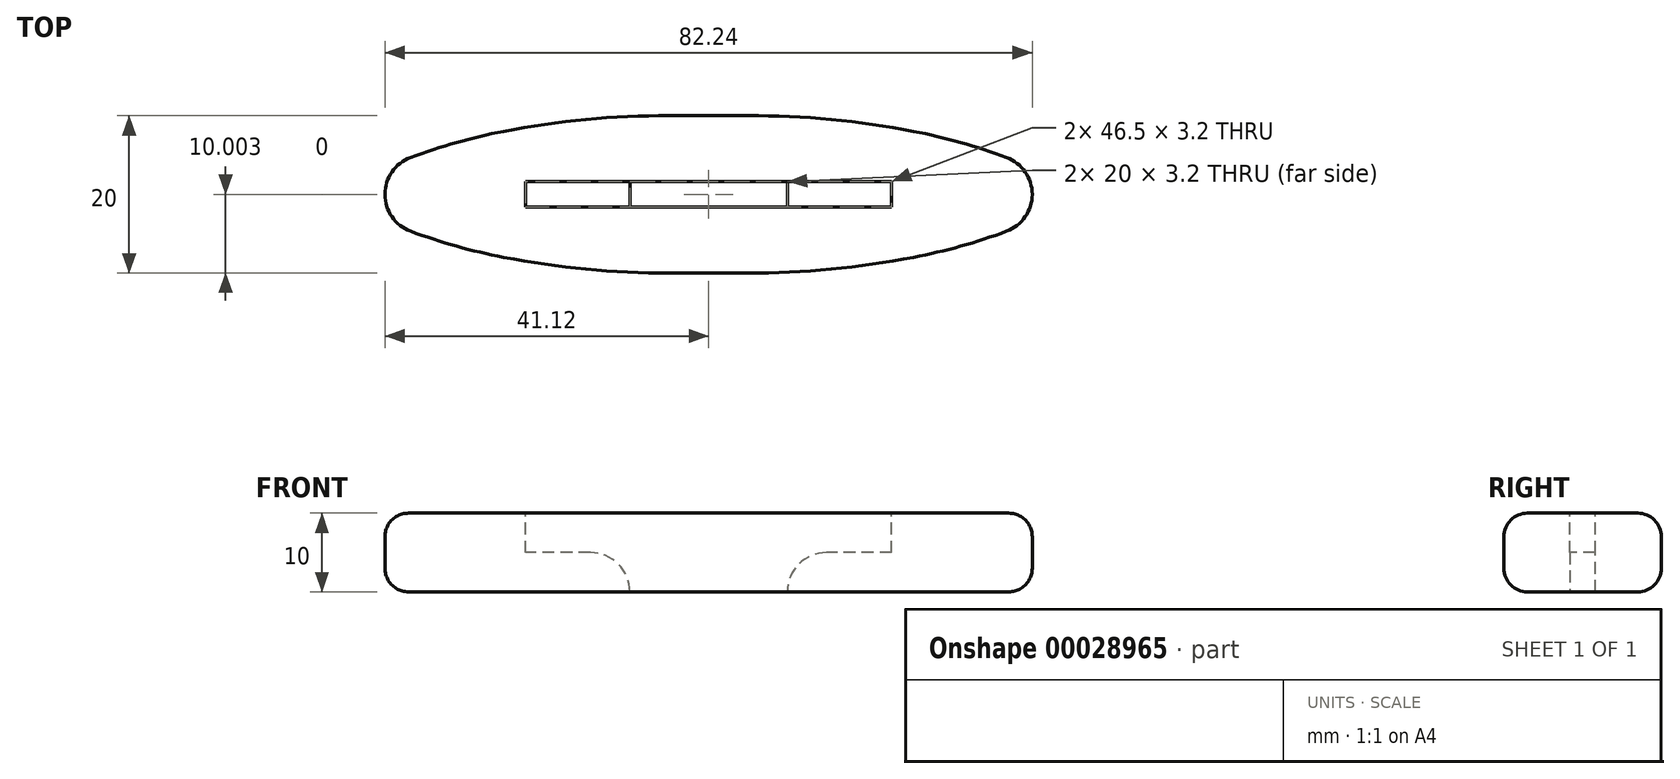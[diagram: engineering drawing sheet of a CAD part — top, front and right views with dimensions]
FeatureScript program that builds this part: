
annotation { "Feature Type Name" : "Feature", "Feature Type Description" : "" }
export const myFeature = defineFeature(function(context is Context, id is Id, definition is map)
    precondition{}
    {
        {
            var Q0;
            Q0=qCreatedBy(makeId("Top.planeOp"),FACE);
            var sketch = newSketch(context, id + "F0", { "sketchPlane" : qUnion([Q0])});
            skLineSegment(sketch, "E0", {"start": v(0, 0) * mm, "end": v(0, 63.05) * mm, "construction": true});
            skPoint(sketch, "E1", {"position": v(0, 31.52) * mm});
            skLineSegment(sketch, "E2.bottom", {"start": v(0, 31.52) * mm, "end": v(-10, 31.52) * mm});
            skLineSegment(sketch, "E2.top", {"start": v(0, 34.72) * mm, "end": v(-10, 34.72) * mm});
            skLineSegment(sketch, "E2.left", {"start": v(0, 31.52) * mm, "end": v(0, 34.72) * mm});
            skLineSegment(sketch, "E2.right", {"start": v(-10, 31.52) * mm, "end": v(-10, 34.72) * mm});
            skPoint(sketch, "E3", {"position": v(0, 33.12) * mm});
            skPoint(sketch, "E4", {"position": v(-48, 33.12) * mm});
            skLineSegment(sketch, "E5", {"start": v(0, 33.12) * mm, "end": v(-68.68, 33.12) * mm, "construction": true});
            skPoint(sketch, "E6", {"position": v(0, 43.12) * mm});
            skPoint(sketch, "E7", {"position": v(-26.03, 41.12) * mm});
            skPoint(sketch, "E8", {"position": v(-5, 43.12) * mm});
            skLineSegment(sketch, "E9", {"start": v(0, 43.12) * mm, "end": v(-5, 43.12) * mm});
            skArc(sketch, "E10", {"start": v(-5, 43.12) * mm, "mid": v(-15.56, 42.62) * mm, "end": v(-26.03, 41.12) * mm});
            skArc(sketch, "E11", {"start": v(-26.03, 41.12) * mm, "mid": v(-37.34, 38) * mm, "end": v(-48, 33.12) * mm});
            skArc(sketch, "E12.MirrorCS", {"start": v(-26.03, 25.12) * mm, "mid": v(-37.34, 28.24) * mm, "end": v(-48, 33.12) * mm});
            skArc(sketch, "E13.MirrorCS", {"start": v(-5, 23.12) * mm, "mid": v(-15.56, 23.62) * mm, "end": v(-26.03, 25.12) * mm});
            skLineSegment(sketch, "E14.MirrorCS", {"start": v(0, 23.12) * mm, "end": v(-5, 23.12) * mm});
            skLineSegment(sketch, "E15.MirrorCS", {"start": v(0, 43.12) * mm, "end": v(5, 43.12) * mm});
            skLineSegment(sketch, "E16.MirrorCS", {"start": v(0, 23.12) * mm, "end": v(5, 23.12) * mm});
            skArc(sketch, "E17.MirrorCS", {"start": v(5, 23.12) * mm, "mid": v(15.56, 23.62) * mm, "end": v(26.03, 25.12) * mm});
            skArc(sketch, "E18.MirrorCS", {"start": v(26.03, 25.12) * mm, "mid": v(37.34, 28.24) * mm, "end": v(48, 33.12) * mm});
            skArc(sketch, "E19.MirrorCS", {"start": v(26.03, 41.12) * mm, "mid": v(37.34, 38) * mm, "end": v(48, 33.12) * mm});
            skArc(sketch, "E20.MirrorCS", {"start": v(5, 43.12) * mm, "mid": v(15.56, 42.62) * mm, "end": v(26.03, 41.12) * mm});
            skLineSegment(sketch, "E21.MirrorCS", {"start": v(0, 34.72) * mm, "end": v(10, 34.72) * mm});
            skLineSegment(sketch, "E22.MirrorCS", {"start": v(10, 31.52) * mm, "end": v(10, 34.72) * mm});
            skLineSegment(sketch, "E23.MirrorCS", {"start": v(0, 31.52) * mm, "end": v(10, 31.52) * mm});
            skSolve(sketch);
        }
        {
            var Q0;
            Q0=makeQuery(id+"F0.imprint","IMPRINT",FACE,{"disambiguationData":[TD([[makeQuery(id+"F0.imprint","IMPRINT",EDGE,{"derivedFrom":sQuery(id+"F0.wireOp",EDGE,"E2.bottom")}),1.0]])]});
            extrude(context, id + "F1", {"entities" : qUnion([Q0]), "depth" : 10 * mm});
        }
        {
            var Q0;
            Q0=makeQuery(id+"F1.opExtrude","SWEPT_EDGE",EDGE,{"disambiguationData":[OSD([sQuery(id+"F0.wireOp",EDGE,"E11"),sQuery(id+"F0.wireOp",EDGE,"E12.MirrorCS")])]});
            var Q1;
            Q1=makeQuery(id+"F1.opExtrude","SWEPT_EDGE",EDGE,{"disambiguationData":[OSD([sQuery(id+"F0.wireOp",EDGE,"E18.MirrorCS"),sQuery(id+"F0.wireOp",EDGE,"E19.MirrorCS")])]});
            fillet(context, id + "F2", {"entities" : qUnion([Q0, Q1]), "radius" : 5 * mm, "tangentPropagation" : true, "allowEdgeOverflow" : false});
        }
        {
            var Q0;
            Q0=makeQuery(id+"F1.opExtrude","CAP_FACE",FACE,{"disambiguationData":[OSD([sQuery(id+"F0.wireOp",EDGE,"E2.bottom"),sQuery(id+"F0.wireOp",EDGE,"E2.top"),sQuery(id+"F0.wireOp",EDGE,"E2.right"),sQuery(id+"F0.wireOp",EDGE,"E9"),sQuery(id+"F0.wireOp",EDGE,"E10"),sQuery(id+"F0.wireOp",EDGE,"E11"),sQuery(id+"F0.wireOp",EDGE,"E12.MirrorCS"),sQuery(id+"F0.wireOp",EDGE,"E13.MirrorCS"),sQuery(id+"F0.wireOp",EDGE,"E14.MirrorCS"),sQuery(id+"F0.wireOp",EDGE,"E15.MirrorCS"),sQuery(id+"F0.wireOp",EDGE,"E16.MirrorCS"),sQuery(id+"F0.wireOp",EDGE,"E17.MirrorCS"),sQuery(id+"F0.wireOp",EDGE,"E18.MirrorCS"),sQuery(id+"F0.wireOp",EDGE,"E19.MirrorCS"),sQuery(id+"F0.wireOp",EDGE,"E20.MirrorCS"),sQuery(id+"F0.wireOp",EDGE,"E21.MirrorCS"),sQuery(id+"F0.wireOp",EDGE,"E22.MirrorCS"),sQuery(id+"F0.wireOp",EDGE,"E23.MirrorCS")])],"isStart":false});
            var sketch = newSketch(context, id + "F3", { "sketchPlane" : qUnion([Q0])});
            skLineSegment(sketch, "E24", {"start": v(0, 34.72) * mm, "end": v(0, 31.52) * mm, "construction": true});
            skLineSegment(sketch, "E25.bottom", {"start": v(0, 34.72) * mm, "end": v(-23.25, 34.72) * mm});
            skLineSegment(sketch, "E25.top", {"start": v(0, 31.52) * mm, "end": v(-23.25, 31.52) * mm});
            skLineSegment(sketch, "E25.left", {"start": v(0, 34.72) * mm, "end": v(0, 31.52) * mm});
            skLineSegment(sketch, "E25.right", {"start": v(-23.25, 34.72) * mm, "end": v(-23.25, 31.52) * mm});
            skLineSegment(sketch, "E26.MirrorCS", {"start": v(0, 34.72) * mm, "end": v(23.25, 34.72) * mm});
            skLineSegment(sketch, "E27.MirrorCS", {"start": v(23.25, 34.72) * mm, "end": v(23.25, 31.52) * mm});
            skLineSegment(sketch, "E28.MirrorCS", {"start": v(0, 31.52) * mm, "end": v(23.25, 31.52) * mm});
            skSolve(sketch);
        }
        {
            var Q0;
            {var subQ2=sQuery(id+"F3.wireOp",EDGE,"E25.right");Q0=makeQuery(id+"F3.imprint","IMPRINT",FACE,{"disambiguationData":[TD([[makeQuery(id+"F3.imprint","IMPRINT",EDGE,{"derivedFrom":subQ2}),1.0]])]});}
            var Q1;
            {var subQ2=sQuery(id+"F3.wireOp",EDGE,"E27.MirrorCS");Q1=makeQuery(id+"F3.imprint","IMPRINT",FACE,{"disambiguationData":[TD([[makeQuery(id+"F3.imprint","IMPRINT",EDGE,{"derivedFrom":subQ2}),-1.0]])]});}
            var Q2;
            {var subQ2=sQuery(id+"F3.wireOp",EDGE,"E25.left");Q2=makeQuery(id+"F3.imprint","IMPRINT",FACE,{"disambiguationData":[TD([[makeQuery(id+"F3.imprint","IMPRINT",EDGE,{"derivedFrom":subQ2}),-1.0]])]});}
            var Q3;
            {var subQ0=sQuery(id+"F3.wireOp",EDGE,"E25.left");Q3=makeQuery(id+"F3.imprint","IMPRINT",FACE,{"disambiguationData":[TD([[makeQuery(id+"F3.imprint","IMPRINT",EDGE,{"derivedFrom":subQ0}),1.0]])]});}
            extrude(context, id + "F4", {"entities" : qUnion([Q0, Q1, Q2, Q3]), "operationType" : NewBodyOperationType.REMOVE, "oppositeDirection" : true, "depth" : 5 * mm});
        }
        {
            var Q0;
            Q0=makeQuery(id+"F4.boolean.opBoolean","INTERSECT",EDGE,{"derivedFrom":[makeQuery(id+"F1.opExtrude","SWEPT_FACE",FACE,{"disambiguationData":[OSD([sQuery(id+"F0.wireOp",EDGE,"E2.right")])]}),makeQuery(id+"F4.opExtrude","CAP_FACE",FACE,{"disambiguationData":[OSD([sQuery(id+"F3.wireOp",EDGE,"E25.bottom"),sQuery(id+"F3.wireOp",EDGE,"E25.top"),sQuery(id+"F3.wireOp",EDGE,"E25.right"),sQuery(id+"F3.wireOp",EDGE,"E26.MirrorCS"),sQuery(id+"F3.wireOp",EDGE,"E27.MirrorCS"),sQuery(id+"F3.wireOp",EDGE,"E28.MirrorCS")])],"isStart":false})]});
            var Q1;
            Q1=makeQuery(id+"F4.boolean.opBoolean","INTERSECT",EDGE,{"derivedFrom":[makeQuery(id+"F1.opExtrude","SWEPT_FACE",FACE,{"disambiguationData":[OSD([sQuery(id+"F0.wireOp",EDGE,"E22.MirrorCS")])]}),makeQuery(id+"F4.opExtrude","CAP_FACE",FACE,{"disambiguationData":[OSD([sQuery(id+"F3.wireOp",EDGE,"E25.bottom"),sQuery(id+"F3.wireOp",EDGE,"E25.top"),sQuery(id+"F3.wireOp",EDGE,"E25.right"),sQuery(id+"F3.wireOp",EDGE,"E26.MirrorCS"),sQuery(id+"F3.wireOp",EDGE,"E27.MirrorCS"),sQuery(id+"F3.wireOp",EDGE,"E28.MirrorCS")])],"isStart":false})]});
            fillet(context, id + "F5", {"entities" : qUnion([Q0, Q1]), "radius" : 5 * mm, "tangentPropagation" : true, "allowEdgeOverflow" : false});
        }
        {
            var Q0;
            Q0=makeQuery(id+"F1.opExtrude","CAP_EDGE",EDGE,{"disambiguationData":[OSD([sQuery(id+"F0.wireOp",EDGE,"E13.MirrorCS")])],"isStart":false});
            var Q1;
            Q1=makeQuery(id+"F1.opExtrude","CAP_EDGE",EDGE,{"disambiguationData":[OSD([sQuery(id+"F0.wireOp",EDGE,"E14.MirrorCS"),sQuery(id+"F0.wireOp",EDGE,"E16.MirrorCS")])],"isStart":true});
            fillet(context, id + "F6", {"entities" : qUnion([Q0, Q1]), "radius" : 3 * mm, "tangentPropagation" : true, "allowEdgeOverflow" : false});
        }
    });
